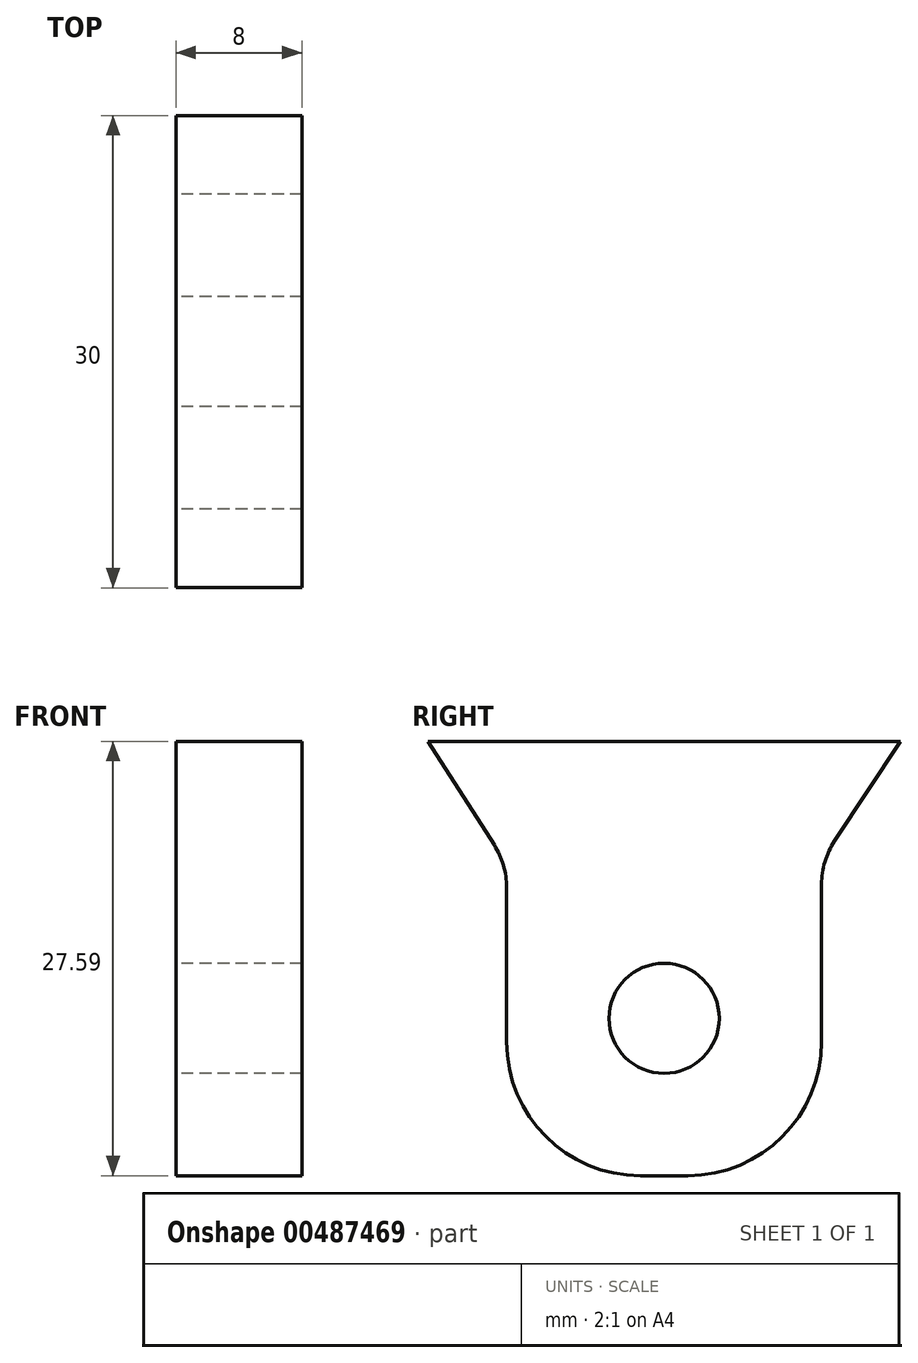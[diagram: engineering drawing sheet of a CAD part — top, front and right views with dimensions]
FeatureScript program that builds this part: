
annotation { "Feature Type Name" : "Feature", "Feature Type Description" : "" }
export const myFeature = defineFeature(function(context is Context, id is Id, definition is map)
    precondition{}
    {
        {
            var Q0;
            Q0=qCreatedBy(makeId("Right.planeOp"),FACE);
            var sketch = newSketch(context, id + "F0", { "sketchPlane" : qUnion([Q0])});
            skLineSegment(sketch, "E0", {"start": v(-50.27, 46.74) * mm, "end": v(-20.27, 46.74) * mm});
            skLineSegment(sketch, "E1", {"start": v(-20.27, 46.74) * mm, "end": v(-24.44, 40.4) * mm});
            skLineSegment(sketch, "E2", {"start": v(-25.27, 37.65) * mm, "end": v(-25.27, 27.65) * mm});
            skLineSegment(sketch, "E3", {"start": v(-33.77, 19.15) * mm, "end": v(-36.77, 19.15) * mm});
            skLineSegment(sketch, "E4", {"start": v(-45.27, 27.65) * mm, "end": v(-45.27, 37.46) * mm});
            skLineSegment(sketch, "E5", {"start": v(-46.05, 40.15) * mm, "end": v(-50.27, 46.74) * mm});
            skCircle(sketch, "E6", {"center": v(-35.27, 29.15) * mm, "radius": 3.5 * mm});
            skPoint(sketch, "E7.visualSharp", {"position": v(-25.27, 19.15) * mm});
            skArc(sketch, "E7.filletArc", {"start": v(-33.77, 19.15) * mm, "mid": v(-27.76, 21.63) * mm, "end": v(-25.27, 27.65) * mm});
            skPoint(sketch, "E8.visualSharp", {"position": v(-45.27, 19.15) * mm});
            skArc(sketch, "E8.filletArc", {"start": v(-45.27, 27.65) * mm, "mid": v(-42.78, 21.63) * mm, "end": v(-36.77, 19.15) * mm});
            skPoint(sketch, "E9.visualSharp", {"position": v(-45.27, 38.92) * mm});
            skArc(sketch, "E9.filletArc", {"start": v(-45.27, 37.46) * mm, "mid": v(-45.47, 38.86) * mm, "end": v(-46.05, 40.15) * mm});
            skPoint(sketch, "E10.visualSharp", {"position": v(-25.27, 39.15) * mm});
            skArc(sketch, "E10.filletArc", {"start": v(-24.44, 40.4) * mm, "mid": v(-25.06, 39.08) * mm, "end": v(-25.27, 37.65) * mm});
            skSolve(sketch);
        }
        {
            var Q0;
            Q0 = qSketchRegion(id + "F0", true);
            extrude(context, id + "F1", {"entities" : qUnion([Q0]), "depth" : 4 * mm, "hasSecondDirection" : true, "secondDirectionOppositeDirection" : true, "secondDirectionDepth" : 4 * mm});
        }
    });
